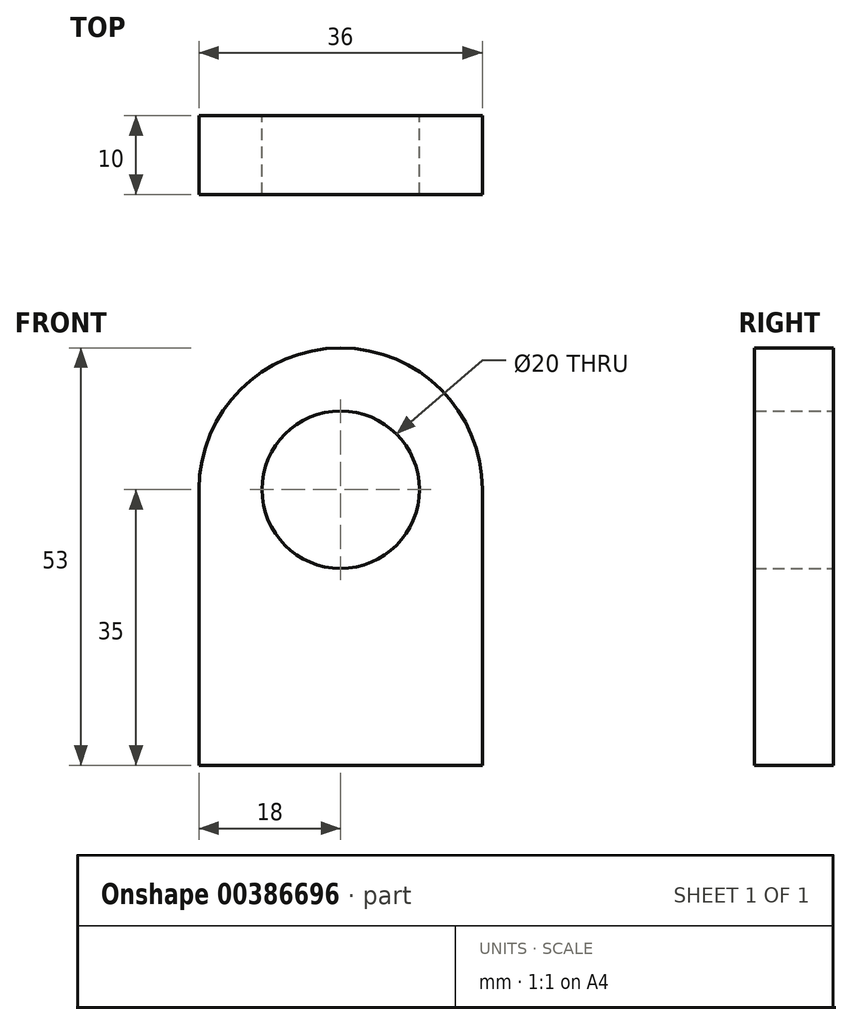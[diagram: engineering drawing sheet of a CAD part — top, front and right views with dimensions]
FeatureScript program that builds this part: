
annotation { "Feature Type Name" : "Feature", "Feature Type Description" : "" }
export const myFeature = defineFeature(function(context is Context, id is Id, definition is map)
    precondition{}
    {
        {
            var Q0;
            Q0=qCreatedBy(makeId("Front.planeOp"),FACE);
            var sketch = newSketch(context, id + "F0", { "sketchPlane" : qUnion([Q0])});
            skCircle(sketch, "E0", {"center": v(0, 35) * mm, "radius": 10 * mm});
            skLineSegment(sketch, "E1", {"start": v(-18, 35) * mm, "end": v(-18, 0) * mm});
            skLineSegment(sketch, "E2", {"start": v(18, 35) * mm, "end": v(18, 0) * mm});
            skLineSegment(sketch, "E3", {"start": v(18, 0) * mm, "end": v(-18, 0) * mm});
            skArc(sketch, "E4", {"start": v(18, 35) * mm, "mid": v(0, 53) * mm, "end": v(-18, 35) * mm});
            skCircle(sketch, "E5", {"center": v(-23.68, -23.23) * mm, "radius": 10 * mm});
            skLineSegment(sketch, "E6", {"start": v(-41.68, -23.23) * mm, "end": v(-41.68, -58.23) * mm});
            skLineSegment(sketch, "E7", {"start": v(-5.68, -23.23) * mm, "end": v(-5.68, -58.23) * mm});
            skLineSegment(sketch, "E8", {"start": v(-5.68, -58.23) * mm, "end": v(-41.68, -58.23) * mm});
            skArc(sketch, "E9", {"start": v(-5.68, -23.23) * mm, "mid": v(-23.68, -5.23) * mm, "end": v(-41.68, -23.23) * mm});
            skCircle(sketch, "E10", {"center": v(46.78, -23.82) * mm, "radius": 10 * mm});
            skLineSegment(sketch, "E11", {"start": v(28.78, -23.82) * mm, "end": v(28.78, -58.82) * mm});
            skLineSegment(sketch, "E12", {"start": v(64.78, -23.82) * mm, "end": v(64.78, -58.82) * mm});
            skLineSegment(sketch, "E13", {"start": v(64.78, -58.82) * mm, "end": v(28.78, -58.82) * mm});
            skArc(sketch, "E14", {"start": v(64.78, -23.82) * mm, "mid": v(46.78, -5.82) * mm, "end": v(28.78, -23.82) * mm});
            skSolve(sketch);
        }
        {
            var Q0;
            Q0=makeQuery(id+"F0.imprint","IMPRINT",FACE,{"disambiguationData":[TD([[makeQuery(id+"F0.imprint","IMPRINT",EDGE,{"derivedFrom":sQuery(id+"F0.wireOp",EDGE,"E0")}),-1.0]])]});
            extrude(context, id + "F1", {"entities" : qUnion([Q0]), "depth" : 10 * mm});
        }
    });
